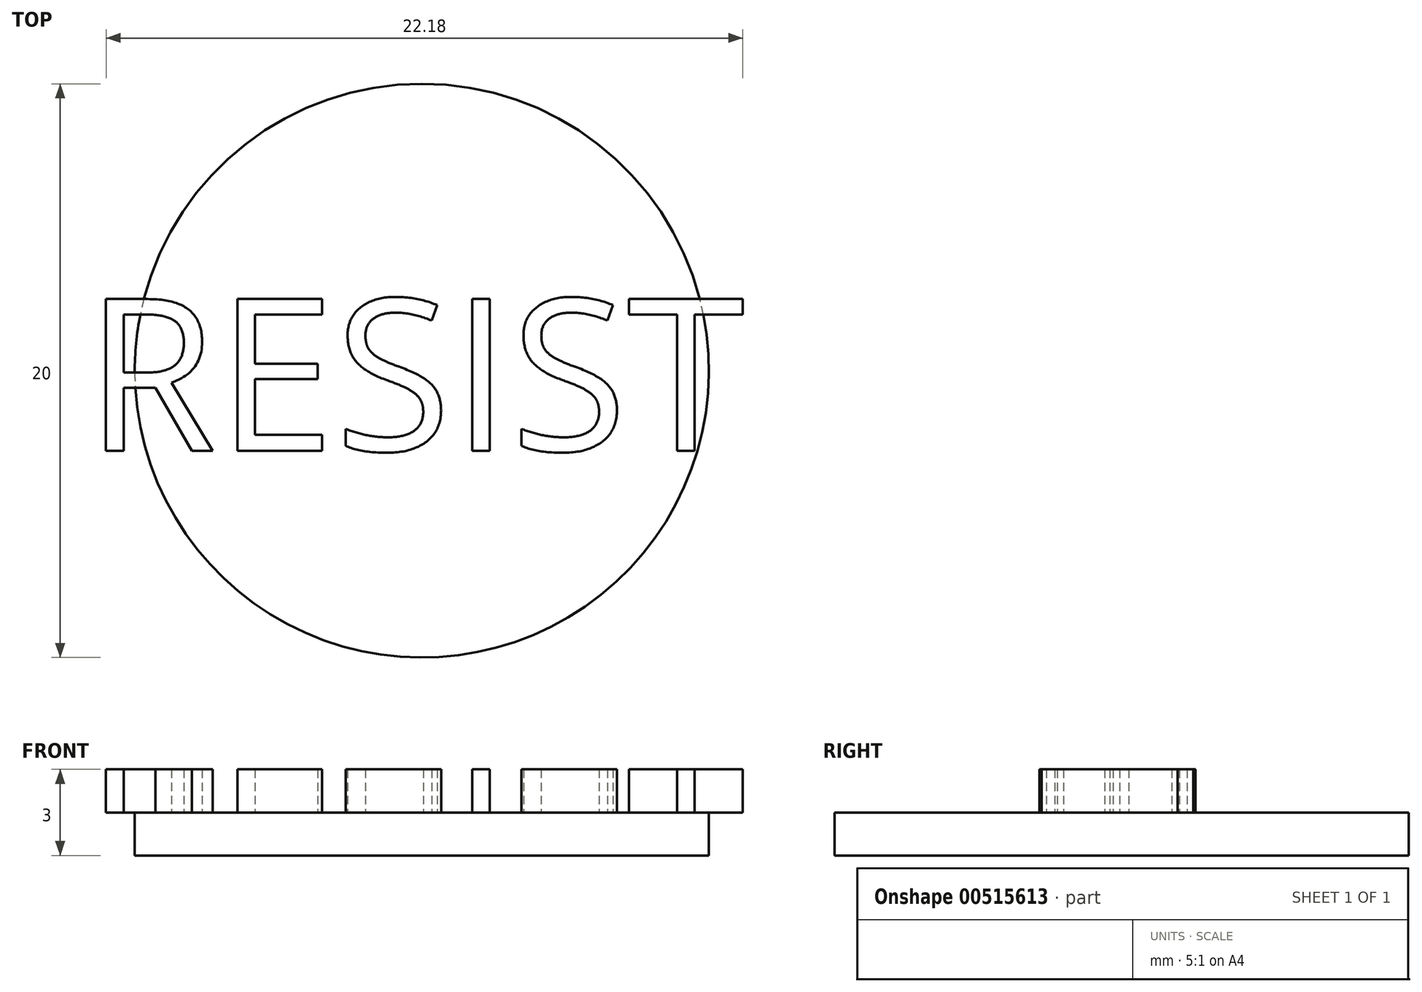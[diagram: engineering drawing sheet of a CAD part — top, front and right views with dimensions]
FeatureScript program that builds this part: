
annotation { "Feature Type Name" : "Feature", "Feature Type Description" : "" }
export const myFeature = defineFeature(function(context is Context, id is Id, definition is map)
    precondition{}
    {
        {
            var Q0;
            Q0=qCreatedBy(makeId("Top.planeOp"),FACE);
            var sketch = newSketch(context, id + "F0", { "sketchPlane" : qUnion([Q0])});
            skCircle(sketch, "E0", {"center": v(0, 0) * mm, "radius": 10 * mm});
            skLineSegment(sketch, "E1", {"start": v(0, 0) * mm, "end": v(10, 0) * mm});
            skSolve(sketch);
        }
        {
            var Q0;
            Q0 = qSketchRegion(id + "F0", true);
            extrude(context, id + "F1", {"entities" : qUnion([Q0]), "depth" : 1.5 * mm, "offsetDistance" : 25 * mm});
        }
        {
            var Q0;
            Q0=makeQuery(id+"F1.opExtrude","CAP_FACE",FACE,{"disambiguationData":[OSD([sQuery(id+"F0.wireOp",EDGE,"E0")])],"isStart":false});
            var sketch = newSketch(context, id + "F2", { "sketchPlane" : qUnion([Q0])});
            skText(sketch, "E2", { "text": "RESIST", "fontName": "OpenSans-Regular.ttf"});
            const initialGuessF2  = {"E2": [-0.01173, -0.00279, 1, 0, 0.00533]};
            skSetInitialGuess(sketch, initialGuessF2);
            skSolve(sketch);
        }
        {
            var Q0;
            Q0 = qSketchRegion(id + "F2", true);
            extrude(context, id + "F3", {"entities" : qUnion([Q0]), "operationType" : NewBodyOperationType.ADD, "depth" : 1.5 * mm, "offsetDistance" : 25 * mm});
        }
    });
